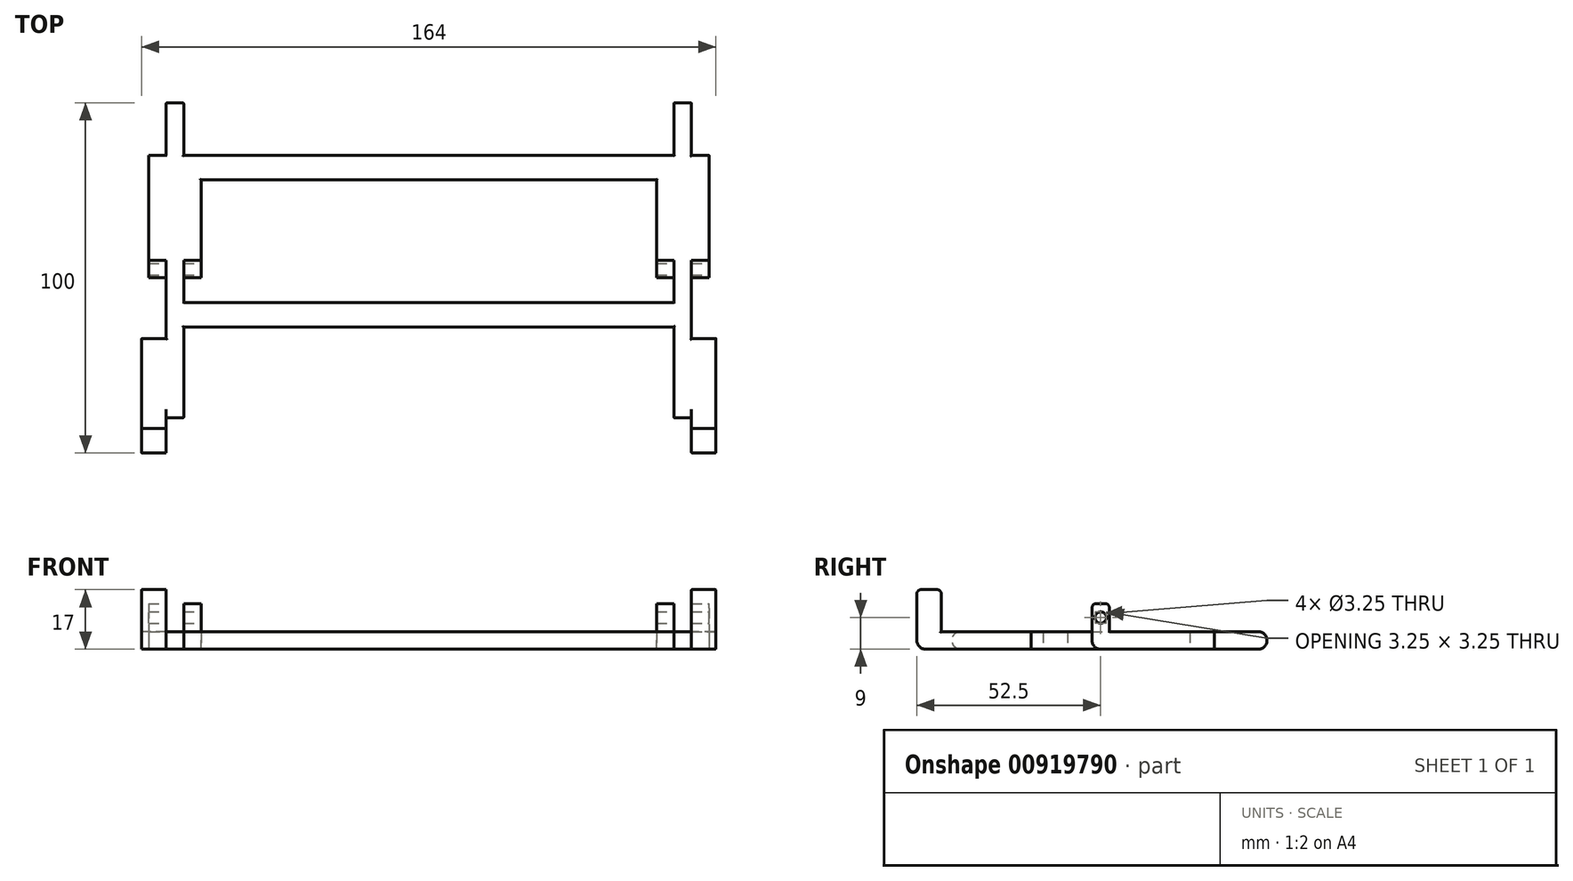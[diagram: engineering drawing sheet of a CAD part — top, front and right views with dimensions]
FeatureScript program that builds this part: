
annotation { "Feature Type Name" : "Feature", "Feature Type Description" : "" }
export const myFeature = defineFeature(function(context is Context, id is Id, definition is map)
    precondition{}
    {
        {
            var Q0;
            Q0=qCreatedBy(makeId("Top.planeOp"),FACE);
            var sketch = newSketch(context, id + "F0", { "sketchPlane" : qUnion([Q0])});
            skLineSegment(sketch, "E0", {"start": v(0, 72) * mm, "end": v(0, 0) * mm, "construction": true});
            skLineSegment(sketch, "E1", {"start": v(-75, 10) * mm, "end": v(-75, 85) * mm});
            skLineSegment(sketch, "E2", {"start": v(-70, 85) * mm, "end": v(-70, 10) * mm});
            skLineSegment(sketch, "E3", {"start": v(-70, 10) * mm, "end": v(-75, 10) * mm});
            skLineSegment(sketch, "E4", {"start": v(-70, 85) * mm, "end": v(0, 85) * mm});
            skLineSegment(sketch, "E5", {"start": v(0, 78) * mm, "end": v(-70, 78) * mm});
            skLineSegment(sketch, "E6", {"start": v(-75, 85) * mm, "end": v(-75, 100) * mm});
            skLineSegment(sketch, "E7", {"start": v(-75, 100) * mm, "end": v(-70, 100) * mm});
            skLineSegment(sketch, "E8", {"start": v(-70, 100) * mm, "end": v(-70, 85) * mm});
            skLineSegment(sketch, "E9", {"start": v(-75, 32.66) * mm, "end": v(-82, 32.66) * mm});
            skLineSegment(sketch, "E10", {"start": v(-82, 32.66) * mm, "end": v(-82, 0) * mm});
            skLineSegment(sketch, "E11", {"start": v(-82, 0) * mm, "end": v(-75, 0) * mm});
            skLineSegment(sketch, "E12", {"start": v(-75, 0) * mm, "end": v(-75, 10) * mm});
            skLineSegment(sketch, "E13", {"start": v(-75, 85) * mm, "end": v(-80, 85) * mm});
            skLineSegment(sketch, "E14", {"start": v(-80, 85) * mm, "end": v(-80, 50) * mm});
            skLineSegment(sketch, "E15", {"start": v(-80, 50) * mm, "end": v(-75, 50) * mm});
            skLineSegment(sketch, "E16", {"start": v(-70, 50) * mm, "end": v(-65, 50) * mm});
            skLineSegment(sketch, "E17", {"start": v(-65, 50) * mm, "end": v(-65, 78) * mm});
            skLineSegment(sketch, "E18.MirrorCS", {"start": v(0, 78) * mm, "end": v(70, 78) * mm});
            skLineSegment(sketch, "E19.MirrorCS", {"start": v(70, 85) * mm, "end": v(0, 85) * mm});
            skLineSegment(sketch, "E20.MirrorCS", {"start": v(65, 50) * mm, "end": v(65, 78) * mm});
            skLineSegment(sketch, "E21.MirrorCS", {"start": v(70, 100) * mm, "end": v(70, 85) * mm});
            skLineSegment(sketch, "E22.MirrorCS", {"start": v(70, 10) * mm, "end": v(75, 10) * mm});
            skLineSegment(sketch, "E23.MirrorCS", {"start": v(82, 32.66) * mm, "end": v(82, 0) * mm});
            skLineSegment(sketch, "E24.MirrorCS", {"start": v(75, 100) * mm, "end": v(70, 100) * mm});
            skLineSegment(sketch, "E25.MirrorCS", {"start": v(75, 10) * mm, "end": v(75, 85) * mm});
            skLineSegment(sketch, "E26.MirrorCS", {"start": v(70, 85) * mm, "end": v(70, 10) * mm});
            skLineSegment(sketch, "E27.MirrorCS", {"start": v(75, 0) * mm, "end": v(75, 10) * mm});
            skLineSegment(sketch, "E28.MirrorCS", {"start": v(80, 85) * mm, "end": v(80, 50) * mm});
            skLineSegment(sketch, "E29.MirrorCS", {"start": v(75, 85) * mm, "end": v(80, 85) * mm});
            skLineSegment(sketch, "E30.MirrorCS", {"start": v(75, 32.66) * mm, "end": v(82, 32.66) * mm});
            skLineSegment(sketch, "E31.MirrorCS", {"start": v(70, 50) * mm, "end": v(65, 50) * mm});
            skLineSegment(sketch, "E32.MirrorCS", {"start": v(80, 50) * mm, "end": v(75, 50) * mm});
            skLineSegment(sketch, "E33.MirrorCS", {"start": v(75, 85) * mm, "end": v(75, 100) * mm});
            skLineSegment(sketch, "E34.MirrorCS", {"start": v(82, 0) * mm, "end": v(75, 0) * mm});
            skLineSegment(sketch, "E35", {"start": v(-70, 43) * mm, "end": v(0, 43) * mm});
            skLineSegment(sketch, "E36", {"start": v(0, 36) * mm, "end": v(-70, 36) * mm});
            skLineSegment(sketch, "E37.MirrorCS", {"start": v(70, 43) * mm, "end": v(0, 43) * mm});
            skLineSegment(sketch, "E38.MirrorCS", {"start": v(0, 36) * mm, "end": v(70, 36) * mm});
            skSolve(sketch);
        }
        {
            var Q0;
            Q0 = qSketchRegion(id + "F0", true);
            var Q1;
            {var subQ3=sQuery(id+"F0.wireOp",EDGE,"E16");Q1=makeQuery(id+"F0.imprint","IMPRINT",FACE,{"disambiguationData":[TD([[makeQuery(id+"F0.imprint","IMPRINT",EDGE,{"derivedFrom":subQ3}),1.0]])]});}
            var Q2;
            {var subQ3=sQuery(id+"F0.wireOp",EDGE,"E20.MirrorCS");Q2=makeQuery(id+"F0.imprint","IMPRINT",FACE,{"disambiguationData":[TD([[makeQuery(id+"F0.imprint","IMPRINT",EDGE,{"derivedFrom":subQ3}),-1.0]])]});}
            extrude(context, id + "F1", {"entities" : qUnion([Q0, Q1, Q2]), "depth" : 5 * mm, "offsetDistance" : 25 * mm});
        }
        {
            var Q0;
            Q0=makeQuery(id+"F1.opExtrude","CAP_EDGE",EDGE,{"disambiguationData":[OSD([sQuery(id+"F0.wireOp",EDGE,"E7")])],"isStart":false});
            var Q1;
            Q1=makeQuery(id+"F1.opExtrude","CAP_EDGE",EDGE,{"disambiguationData":[OSD([sQuery(id+"F0.wireOp",EDGE,"E7")])],"isStart":true});
            var Q2;
            Q2=makeQuery(id+"F1.opExtrude","CAP_EDGE",EDGE,{"disambiguationData":[OSD([sQuery(id+"F0.wireOp",EDGE,"E24.MirrorCS")])],"isStart":true});
            var Q3;
            Q3=makeQuery(id+"F1.opExtrude","CAP_EDGE",EDGE,{"disambiguationData":[OSD([sQuery(id+"F0.wireOp",EDGE,"E24.MirrorCS")])],"isStart":false});
            var Q4;
            Q4=makeQuery(id+"F1.opExtrude","CAP_EDGE",EDGE,{"disambiguationData":[OSD([sQuery(id+"F0.wireOp",EDGE,"E11")])],"isStart":true});
            var Q5;
            Q5=makeQuery(id+"F1.opExtrude","CAP_EDGE",EDGE,{"disambiguationData":[OSD([sQuery(id+"F0.wireOp",EDGE,"E34.MirrorCS")])],"isStart":true});
            var Q6;
            Q6=makeQuery(id+"F1.opExtrude","CAP_EDGE",EDGE,{"disambiguationData":[OSD([sQuery(id+"F0.wireOp",EDGE,"E3")])],"isStart":true});
            var Q7;
            Q7=makeQuery(id+"F1.opExtrude","CAP_EDGE",EDGE,{"disambiguationData":[OSD([sQuery(id+"F0.wireOp",EDGE,"E22.MirrorCS")])],"isStart":true});
            var Q8;
            Q8=makeQuery(id+"F1.opExtrude","CAP_EDGE",EDGE,{"disambiguationData":[OSD([sQuery(id+"F0.wireOp",EDGE,"E31.MirrorCS")])],"isStart":true});
            var Q9;
            Q9=makeQuery(id+"F1.opExtrude","CAP_EDGE",EDGE,{"disambiguationData":[OSD([sQuery(id+"F0.wireOp",EDGE,"E32.MirrorCS")])],"isStart":true});
            var Q10;
            Q10=makeQuery(id+"F1.opExtrude","CAP_EDGE",EDGE,{"disambiguationData":[OSD([sQuery(id+"F0.wireOp",EDGE,"E16")])],"isStart":true});
            var Q11;
            Q11=makeQuery(id+"F1.opExtrude","CAP_EDGE",EDGE,{"disambiguationData":[OSD([sQuery(id+"F0.wireOp",EDGE,"E15")])],"isStart":true});
            var Q12;
            Q12=makeQuery(id+"F1.opExtrude","CAP_EDGE",EDGE,{"disambiguationData":[OSD([sQuery(id+"F0.wireOp",EDGE,"E22.MirrorCS")])],"isStart":false});
            var Q13;
            Q13=makeQuery(id+"F1.opExtrude","CAP_EDGE",EDGE,{"disambiguationData":[OSD([sQuery(id+"F0.wireOp",EDGE,"E3")])],"isStart":false});
            fillet(context, id + "F2", {"entities" : qUnion([Q0, Q1, Q2, Q3, Q4, Q5, Q6, Q7, Q8, Q9, Q10, Q11, Q12, Q13]), "radius" : 2.5 * mm, "tangentPropagation" : true, "allowEdgeOverflow" : false});
        }
        {
            var Q0;
            Q0=makeQuery(id+"F1.opExtrude","CAP_FACE",FACE,{"disambiguationData":[OSD([sQuery(id+"F0.wireOp",EDGE,"E1"),sQuery(id+"F0.wireOp",EDGE,"E2"),sQuery(id+"F0.wireOp",EDGE,"E3"),sQuery(id+"F0.wireOp",EDGE,"E4"),sQuery(id+"F0.wireOp",EDGE,"E5"),sQuery(id+"F0.wireOp",EDGE,"E6"),sQuery(id+"F0.wireOp",EDGE,"E7"),sQuery(id+"F0.wireOp",EDGE,"E8"),sQuery(id+"F0.wireOp",EDGE,"E9"),sQuery(id+"F0.wireOp",EDGE,"E10"),sQuery(id+"F0.wireOp",EDGE,"E11"),sQuery(id+"F0.wireOp",EDGE,"E12"),sQuery(id+"F0.wireOp",EDGE,"E13"),sQuery(id+"F0.wireOp",EDGE,"E14"),sQuery(id+"F0.wireOp",EDGE,"E15"),sQuery(id+"F0.wireOp",EDGE,"E16"),sQuery(id+"F0.wireOp",EDGE,"E17"),sQuery(id+"F0.wireOp",EDGE,"E18.MirrorCS"),sQuery(id+"F0.wireOp",EDGE,"E19.MirrorCS"),sQuery(id+"F0.wireOp",EDGE,"E20.MirrorCS"),sQuery(id+"F0.wireOp",EDGE,"E21.MirrorCS"),sQuery(id+"F0.wireOp",EDGE,"E22.MirrorCS"),sQuery(id+"F0.wireOp",EDGE,"E23.MirrorCS"),sQuery(id+"F0.wireOp",EDGE,"E24.MirrorCS"),sQuery(id+"F0.wireOp",EDGE,"E25.MirrorCS"),sQuery(id+"F0.wireOp",EDGE,"E26.MirrorCS"),sQuery(id+"F0.wireOp",EDGE,"E27.MirrorCS"),sQuery(id+"F0.wireOp",EDGE,"E28.MirrorCS"),sQuery(id+"F0.wireOp",EDGE,"E29.MirrorCS"),sQuery(id+"F0.wireOp",EDGE,"E30.MirrorCS"),sQuery(id+"F0.wireOp",EDGE,"E31.MirrorCS"),sQuery(id+"F0.wireOp",EDGE,"E32.MirrorCS"),sQuery(id+"F0.wireOp",EDGE,"E33.MirrorCS"),sQuery(id+"F0.wireOp",EDGE,"E34.MirrorCS"),sQuery(id+"F0.wireOp",EDGE,"E35"),sQuery(id+"F0.wireOp",EDGE,"E36"),sQuery(id+"F0.wireOp",EDGE,"E37.MirrorCS"),sQuery(id+"F0.wireOp",EDGE,"E38.MirrorCS")])],"isStart":false});
            var sketch = newSketch(context, id + "F3", { "sketchPlane" : qUnion([Q0])});
            skLineSegment(sketch, "E39.bottom", {"start": v(-75, 0) * mm, "end": v(-82, 0) * mm});
            skLineSegment(sketch, "E39.top", {"start": v(-75, 7) * mm, "end": v(-82, 7) * mm});
            skLineSegment(sketch, "E39.left", {"start": v(-75, 0) * mm, "end": v(-75, 7) * mm});
            skLineSegment(sketch, "E39.right", {"start": v(-82, 0) * mm, "end": v(-82, 7) * mm});
            skLineSegment(sketch, "E40.bottom", {"start": v(-80, 50) * mm, "end": v(-75, 50) * mm});
            skLineSegment(sketch, "E40.top", {"start": v(-80, 55) * mm, "end": v(-75, 55) * mm});
            skLineSegment(sketch, "E40.left", {"start": v(-80, 50) * mm, "end": v(-80, 55) * mm});
            skLineSegment(sketch, "E40.right", {"start": v(-75, 50) * mm, "end": v(-75, 55) * mm});
            skLineSegment(sketch, "E41.bottom", {"start": v(-65, 50) * mm, "end": v(-70, 50) * mm});
            skLineSegment(sketch, "E41.top", {"start": v(-65, 55) * mm, "end": v(-70, 55) * mm});
            skLineSegment(sketch, "E41.left", {"start": v(-65, 50) * mm, "end": v(-65, 55) * mm});
            skLineSegment(sketch, "E41.right", {"start": v(-70, 50) * mm, "end": v(-70, 55) * mm});
            skPoint(sketch, "E42.oppositeSnap0", {"position": v(-67.5, 55) * mm});
            skLineSegment(sketch, "E42.bottom", {"start": v(65, 50) * mm, "end": v(70, 50) * mm});
            skLineSegment(sketch, "E42.top", {"start": v(65, 55) * mm, "end": v(70, 55) * mm});
            skLineSegment(sketch, "E42.left", {"start": v(65, 50) * mm, "end": v(65, 55) * mm});
            skLineSegment(sketch, "E42.right", {"start": v(70, 50) * mm, "end": v(70, 55) * mm});
            skLineSegment(sketch, "E43.bottom", {"start": v(75, 50) * mm, "end": v(80, 50) * mm});
            skLineSegment(sketch, "E43.top", {"start": v(75, 55) * mm, "end": v(80, 55) * mm});
            skLineSegment(sketch, "E43.left", {"start": v(75, 50) * mm, "end": v(75, 55) * mm});
            skLineSegment(sketch, "E43.right", {"start": v(80, 50) * mm, "end": v(80, 55) * mm});
            skLineSegment(sketch, "E44.bottom", {"start": v(82, 0) * mm, "end": v(75, 0) * mm});
            skLineSegment(sketch, "E44.top", {"start": v(82, 7) * mm, "end": v(75, 7) * mm});
            skLineSegment(sketch, "E44.left", {"start": v(82, 0) * mm, "end": v(82, 7) * mm});
            skLineSegment(sketch, "E44.right", {"start": v(75, 0) * mm, "end": v(75, 7) * mm});
            skSolve(sketch);
        }
        {
            var Q0;
            Q0=makeQuery(id+"F3.imprint","IMPRINT",FACE,{"disambiguationData":[TD([[makeQuery(id+"F3.imprint","IMPRINT",EDGE,{"derivedFrom":sQuery(id+"F3.wireOp",EDGE,"E40.bottom")}),1.0]])]});
            var Q1;
            Q1=makeQuery(id+"F3.imprint","IMPRINT",FACE,{"disambiguationData":[TD([[makeQuery(id+"F3.imprint","IMPRINT",EDGE,{"derivedFrom":sQuery(id+"F3.wireOp",EDGE,"E41.bottom")}),1.0]])]});
            var Q2;
            Q2=makeQuery(id+"F3.imprint","IMPRINT",FACE,{"disambiguationData":[TD([[makeQuery(id+"F3.imprint","IMPRINT",EDGE,{"derivedFrom":sQuery(id+"F3.wireOp",EDGE,"E42.bottom")}),-1.0]])]});
            var Q3;
            Q3=makeQuery(id+"F3.imprint","IMPRINT",FACE,{"disambiguationData":[TD([[makeQuery(id+"F3.imprint","IMPRINT",EDGE,{"derivedFrom":sQuery(id+"F3.wireOp",EDGE,"E43.bottom")}),-1.0]])]});
            extrude(context, id + "F4", {"entities" : qUnion([Q0, Q1, Q2, Q3]), "operationType" : NewBodyOperationType.ADD, "depth" : 8 * mm, "offsetDistance" : 25 * mm});
        }
        {
            var Q0;
            Q0=makeQuery(id+"F3.imprint","IMPRINT",FACE,{"disambiguationData":[TD([[makeQuery(id+"F3.imprint","IMPRINT",EDGE,{"derivedFrom":sQuery(id+"F3.wireOp",EDGE,"E39.bottom")}),1.0]])]});
            var Q1;
            Q1=makeQuery(id+"F3.imprint","IMPRINT",FACE,{"disambiguationData":[TD([[makeQuery(id+"F3.imprint","IMPRINT",EDGE,{"derivedFrom":sQuery(id+"F3.wireOp",EDGE,"E44.bottom")}),-1.0]])]});
            extrude(context, id + "F5", {"entities" : qUnion([Q0, Q1]), "operationType" : NewBodyOperationType.ADD, "depth" : 12 * mm, "offsetDistance" : 25 * mm});
        }
        {
            var Q0;
            Q0=makeQuery(id+"F4.opExtrude","CAP_EDGE",EDGE,{"disambiguationData":[OSD([sQuery(id+"F3.wireOp",EDGE,"E40.bottom")])],"isStart":false});
            var Q1;
            Q1=makeQuery(id+"F4.opExtrude","CAP_EDGE",EDGE,{"disambiguationData":[OSD([sQuery(id+"F3.wireOp",EDGE,"E40.top")])],"isStart":false});
            var Q2;
            Q2=makeQuery(id+"F4.opExtrude","CAP_EDGE",EDGE,{"disambiguationData":[OSD([sQuery(id+"F3.wireOp",EDGE,"E41.bottom")])],"isStart":false});
            var Q3;
            Q3=makeQuery(id+"F4.opExtrude","CAP_EDGE",EDGE,{"disambiguationData":[OSD([sQuery(id+"F3.wireOp",EDGE,"E41.top")])],"isStart":false});
            var Q4;
            Q4=makeQuery(id+"F5.opExtrude","CAP_EDGE",EDGE,{"disambiguationData":[OSD([sQuery(id+"F3.wireOp",EDGE,"E39.bottom")])],"isStart":false});
            var Q5;
            Q5=makeQuery(id+"F5.opExtrude","CAP_EDGE",EDGE,{"disambiguationData":[OSD([sQuery(id+"F3.wireOp",EDGE,"E39.top")])],"isStart":false});
            var Q6;
            Q6=makeQuery(id+"F5.opExtrude","CAP_EDGE",EDGE,{"disambiguationData":[OSD([sQuery(id+"F3.wireOp",EDGE,"E44.bottom")])],"isStart":false});
            var Q7;
            Q7=makeQuery(id+"F5.opExtrude","CAP_EDGE",EDGE,{"disambiguationData":[OSD([sQuery(id+"F3.wireOp",EDGE,"E44.top")])],"isStart":false});
            var Q8;
            Q8=makeQuery(id+"F4.opExtrude","CAP_EDGE",EDGE,{"disambiguationData":[OSD([sQuery(id+"F3.wireOp",EDGE,"E42.bottom")])],"isStart":false});
            var Q9;
            Q9=makeQuery(id+"F4.opExtrude","CAP_EDGE",EDGE,{"disambiguationData":[OSD([sQuery(id+"F3.wireOp",EDGE,"E42.top")])],"isStart":false});
            var Q10;
            Q10=makeQuery(id+"F4.opExtrude","CAP_EDGE",EDGE,{"disambiguationData":[OSD([sQuery(id+"F3.wireOp",EDGE,"E43.bottom")])],"isStart":false});
            var Q11;
            Q11=makeQuery(id+"F4.opExtrude","CAP_EDGE",EDGE,{"disambiguationData":[OSD([sQuery(id+"F3.wireOp",EDGE,"E43.top")])],"isStart":false});
            fillet(context, id + "F6", {"entities" : qUnion([Q0, Q1, Q2, Q3, Q4, Q5, Q6, Q7, Q8, Q9, Q10, Q11]), "radius" : 1.25 * mm, "tangentPropagation" : true, "allowEdgeOverflow" : false});
        }
        {
            var Q0;
            Q0=makeQuery(id+"F4.boolean.opBoolean","MERGE",FACE,{"derivedFrom":[makeQuery(id+"F1.opExtrude","SWEPT_FACE",FACE,{"disambiguationData":[OSD([sQuery(id+"F0.wireOp",EDGE,"E28.MirrorCS")])]}),makeQuery(id+"F4.opExtrude","SWEPT_FACE",FACE,{"disambiguationData":[OSD([sQuery(id+"F3.wireOp",EDGE,"E43.right")])]})]});
            var sketch = newSketch(context, id + "F7", { "sketchPlane" : qUnion([Q0])});
            skCircle(sketch, "E45", {"center": v(52.5, 9) * mm, "radius": 1.63 * mm});
            skPoint(sketch, "E45.centerSnap0", {"position": v(52.5, 13) * mm});
            skSolve(sketch);
        }
        {
            var Q0;
            Q0 = qSketchRegion(id + "F7", true);
            extrude(context, id + "F8", {"entities" : qUnion([Q0]), "operationType" : NewBodyOperationType.REMOVE, "oppositeDirection" : true, "depth" : 186.3 * mm, "offsetDistance" : 25 * mm});
        }
        {
            var Q0;
            Q0=makeQuery(id+"F1.opExtrude","CAP_EDGE",EDGE,{"disambiguationData":[OSD([sQuery(id+"F0.wireOp",EDGE,"E23.MirrorCS")])],"isStart":false});
            var Q1;
            Q1=makeQuery(id+"F1.opExtrude","CAP_EDGE",EDGE,{"disambiguationData":[OSD([sQuery(id+"F0.wireOp",EDGE,"E28.MirrorCS")])],"isStart":false});
            var Q2;
            Q2=makeQuery(id+"F1.opExtrude","CAP_EDGE",EDGE,{"disambiguationData":[OSD([sQuery(id+"F0.wireOp",EDGE,"E5"),sQuery(id+"F0.wireOp",EDGE,"E18.MirrorCS")])],"isStart":false});
            var Q3;
            Q3=makeQuery(id+"F1.opExtrude","CAP_EDGE",EDGE,{"disambiguationData":[OSD([sQuery(id+"F0.wireOp",EDGE,"E20.MirrorCS")])],"isStart":false});
            var Q4;
            Q4=makeQuery(id+"F1.opExtrude","CAP_EDGE",EDGE,{"disambiguationData":[OSD([sQuery(id+"F0.wireOp",EDGE,"E30.MirrorCS")])],"isStart":false});
            var Q5;
            Q5=makeQuery(id+"F1.opExtrude","CAP_EDGE",EDGE,{"disambiguationData":[OSD([sQuery(id+"F0.wireOp",EDGE,"E17")])],"isStart":false});
            var Q6;
            Q6=makeQuery(id+"F1.opExtrude","CAP_EDGE",EDGE,{"disambiguationData":[OSD([sQuery(id+"F0.wireOp",EDGE,"E14")])],"isStart":false});
            var Q7;
            Q7=makeQuery(id+"F1.opExtrude","CAP_EDGE",EDGE,{"disambiguationData":[OSD([sQuery(id+"F0.wireOp",EDGE,"E1")])],"isStart":false});
            var Q8;
            Q8=makeQuery(id+"F1.opExtrude","CAP_EDGE",EDGE,{"disambiguationData":[OSD([sQuery(id+"F0.wireOp",EDGE,"E10")])],"isStart":false});
            var Q9;
            Q9=makeQuery(id+"F1.opExtrude","CAP_EDGE",EDGE,{"disambiguationData":[OSD([sQuery(id+"F0.wireOp",EDGE,"E9")])],"isStart":false});
            var Q10;
            Q10=makeQuery(id+"F1.opExtrude","CAP_EDGE",EDGE,{"disambiguationData":[OSD([sQuery(id+"F0.wireOp",EDGE,"E29.MirrorCS")])],"isStart":false});
            var Q11;
            Q11=makeQuery(id+"F1.opExtrude","CAP_EDGE",EDGE,{"disambiguationData":[OSD([sQuery(id+"F0.wireOp",EDGE,"E35"),sQuery(id+"F0.wireOp",EDGE,"E37.MirrorCS")])],"isStart":false});
            var Q12;
            Q12=makeQuery(id+"F1.opExtrude","CAP_EDGE",EDGE,{"disambiguationData":[OSD([sQuery(id+"F0.wireOp",EDGE,"E36"),sQuery(id+"F0.wireOp",EDGE,"E38.MirrorCS")])],"isStart":false});
            var Q13;
            Q13=makeQuery(id+"F1.opExtrude","CAP_EDGE",EDGE,{"disambiguationData":[OSD([sQuery(id+"F0.wireOp",EDGE,"E4"),sQuery(id+"F0.wireOp",EDGE,"E19.MirrorCS")])],"isStart":false});
            var Q14;
            Q14=makeQuery(id+"F5.opExtrude","SWEPT_EDGE",EDGE,{"disambiguationData":[OSD([sQuery(id+"F0.wireOp",EDGE,"E23.MirrorCS"),sQuery(id+"F3.wireOp",EDGE,"E44.top"),sQuery(id+"F3.wireOp",EDGE,"E44.left")])]});
            var Q15;
            Q15=makeQuery(id+"F5.boolean.opBoolean","MERGE",EDGE,{"derivedFrom":[makeQuery(id+"F1.opExtrude","SWEPT_EDGE",EDGE,{"disambiguationData":[OSD([sQuery(id+"F0.wireOp",EDGE,"E23.MirrorCS"),sQuery(id+"F0.wireOp",EDGE,"E34.MirrorCS")])]}),makeQuery(id+"F5.opExtrude","SWEPT_EDGE",EDGE,{"disambiguationData":[OSD([sQuery(id+"F3.wireOp",EDGE,"E44.bottom"),sQuery(id+"F3.wireOp",EDGE,"E44.left")])]})]});
            var Q16;
            Q16=makeQuery(id+"F5.boolean.opBoolean","MERGE",EDGE,{"derivedFrom":[makeQuery(id+"F1.opExtrude","SWEPT_EDGE",EDGE,{"disambiguationData":[OSD([sQuery(id+"F0.wireOp",EDGE,"E27.MirrorCS"),sQuery(id+"F0.wireOp",EDGE,"E34.MirrorCS")])]}),makeQuery(id+"F5.opExtrude","SWEPT_EDGE",EDGE,{"disambiguationData":[OSD([sQuery(id+"F3.wireOp",EDGE,"E44.bottom"),sQuery(id+"F3.wireOp",EDGE,"E44.right")])]})]});
            var Q17;
            Q17=makeQuery(id+"F1.opExtrude","CAP_EDGE",EDGE,{"disambiguationData":[OSD([sQuery(id+"F0.wireOp",EDGE,"E25.MirrorCS")])],"isStart":false});
            fillet(context, id + "F9", {"entities" : qUnion([Q0, Q1, Q2, Q3, Q4, Q5, Q6, Q7, Q8, Q9, Q10, Q11, Q12, Q13, Q14, Q15, Q16, Q17]), "radius" : 0.25 * mm, "tangentPropagation" : true, "allowEdgeOverflow" : false});
        }
        {
            var Q0;
            {var subQ0=sQuery(id+"F0.wireOp",EDGE,"E26.MirrorCS");Q0=makeQuery(id+"F1.opExtrude","CAP_EDGE",EDGE,{"disambiguationData":[OSD([subQ0]),TDD([makeQuery(id+"F0.imprint","IMPRINT",EDGE,{"disambiguationData":[TD([[makeQuery(id+"F0.imprint","INTERSECT",VERTEX,{"derivedFrom":[sQuery(id+"F0.wireOp",EDGE,"E22.MirrorCS"),subQ0]}),1.0]])],"derivedFrom":subQ0})])],"isStart":false});}
            var Q1;
            {var subQ0=sQuery(id+"F0.wireOp",EDGE,"E2");Q1=makeQuery(id+"F1.opExtrude","CAP_EDGE",EDGE,{"disambiguationData":[OSD([subQ0]),TDD([makeQuery(id+"F0.imprint","IMPRINT",EDGE,{"disambiguationData":[TD([[makeQuery(id+"F0.imprint","INTERSECT",VERTEX,{"derivedFrom":[subQ0,sQuery(id+"F0.wireOp",EDGE,"E3")]}),1.0]])],"derivedFrom":subQ0})])],"isStart":false});}
            var Q2;
            Q2=makeQuery(id+"F1.opExtrude","CAP_EDGE",EDGE,{"disambiguationData":[OSD([sQuery(id+"F0.wireOp",EDGE,"E33.MirrorCS")])],"isStart":false});
            var Q3;
            Q3=makeQuery(id+"F1.opExtrude","CAP_EDGE",EDGE,{"disambiguationData":[OSD([sQuery(id+"F0.wireOp",EDGE,"E21.MirrorCS")])],"isStart":false});
            var Q4;
            Q4=makeQuery(id+"F1.opExtrude","CAP_EDGE",EDGE,{"disambiguationData":[OSD([sQuery(id+"F0.wireOp",EDGE,"E8")])],"isStart":false});
            var Q5;
            Q5=makeQuery(id+"F1.opExtrude","CAP_EDGE",EDGE,{"disambiguationData":[OSD([sQuery(id+"F0.wireOp",EDGE,"E6")])],"isStart":false});
            fillet(context, id + "F10", {"entities" : qUnion([Q0, Q1, Q2, Q3, Q4, Q5]), "radius" : 0.25 * mm, "tangentPropagation" : true, "allowEdgeOverflow" : false});
        }
    });
